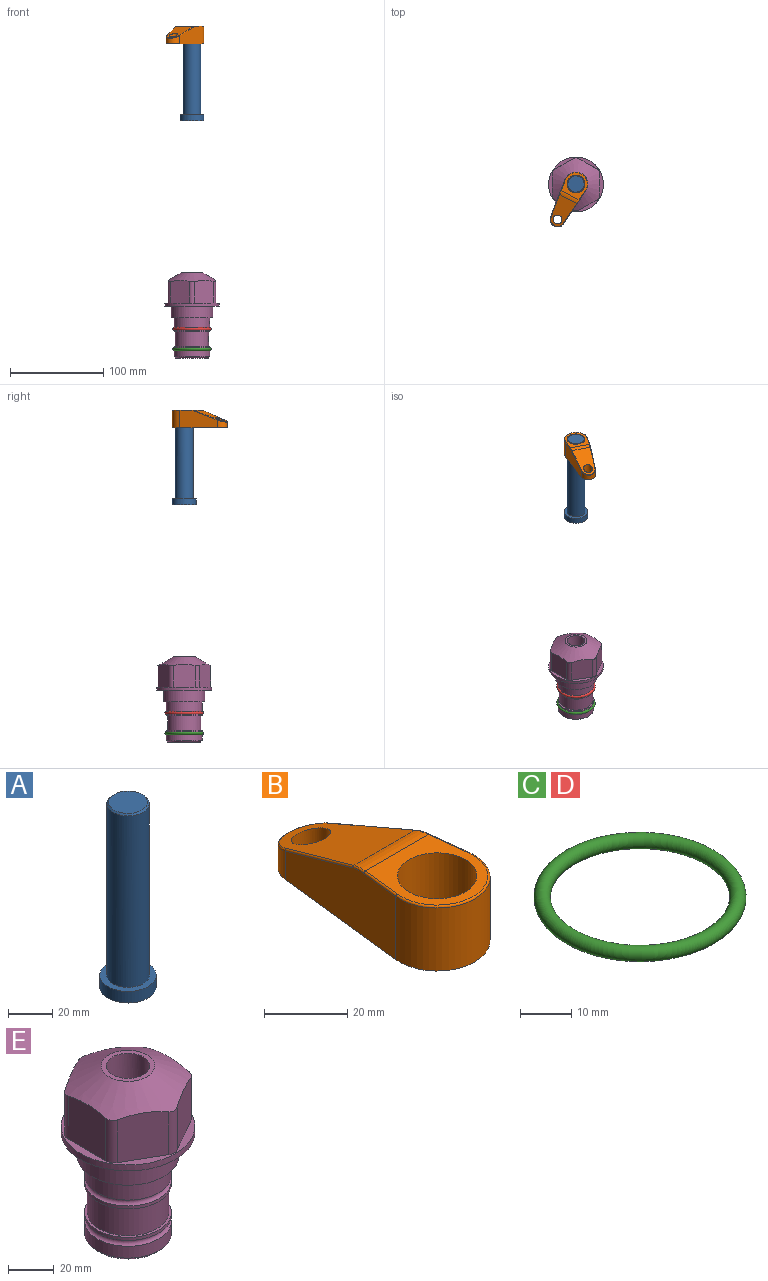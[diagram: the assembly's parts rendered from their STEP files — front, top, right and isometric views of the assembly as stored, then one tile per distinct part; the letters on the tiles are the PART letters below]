
ASSEMBLY  parts=5 mates=3
PART A: 6 faces, bbox 25.4x25.4x101.6 mm
  f0: plane 17.46x17.46mm, normal (0,0,1), area 239.5mm2, adj f5
  f1: plane 25.4x25.4mm, normal (0,0,-1), area 506.7mm2, adj f2
  f2: cylinder r=12.7mm len=25.4mm, axis (0,0,1), area 506.7mm2, adj f1,f3
  f3: plane 25.4x25.4mm, normal (0,0,1), area 221.7mm2, adj f2,f4
  f4: cylinder r=9.53mm len=94.46mm, axis (0,0,1), area 5653mm2, adj f3,f5
  f5: cone r=8.73mm half-angle=45deg, axis (0,0,-1), area 64.4mm2, adj f0,f4
PART B: 44 faces, bbox 27.5x64.5x19.1 mm
  f0: plane 2.3x0.95mm, normal (0,0,-1), area 1mm2, adj f25,f30,f34
  f1: plane 63.5x25.4mm, normal (0,0,-1), area 561.7mm2, adj f2,f3,f4,f5,f6,f7,f19,f20
  f2: cylinder r=12.7mm len=25.4mm, axis (0,0,-1), area 792.2mm2, adj f1,f3,f5,f13
  f3: plane 42.33x18.54mm, normal (0.99,0.11,0), area 647mm2, adj f1,f2,f4,f11,f12,f14
  f4: cylinder r=7.94mm len=15.78mm, axis (0,0,-1), area 158.6mm2, adj f1,f3,f5,f16
  f5: plane 42.33x18.54mm, normal (-0.99,0.11,0), area 647mm2, adj f1,f2,f4,f15,f17,f18
  f6: cylinder r=9.53mm len=19.05mm, axis (0,0,-1), area 1140.1mm2, adj f1,f8
  f7: cylinder r=4.76mm len=10.98mm, axis (0,0,-1), area 276.1mm2, adj f1,f9
  f8: plane 25.83x24.38mm, normal (0,0,1), area 262.2mm2, adj f6,f10,f11,f13,f15
  f9: plane 32.49x20.55mm, normal (0,0.34,0.94), area 489.9mm2, adj f7,f10,f14,f16,f18
  f10: cylinder r=12.7mm len=21.49mm, axis (-1,0,0), area 93.2mm2, adj f8,f9,f12,f17
  f11: cylinder r=0.51mm len=12.34mm, axis (0.11,-0.99,0), area 9.9mm2, adj f3,f8,f12,f13
  f12: bspline ~7.62x1.64mm, area 3.5mm2, adj f3,f10,f11,f14
  f13: torus R=12.19mm, axis (0,0,1), area 33.6mm2, adj f2,f8,f11,f15
  f14: cylinder r=0.51mm len=26.01mm, axis (0.1,-0.93,0.34), area 21.6mm2, adj f3,f9,f12,f16
  f15: cylinder r=0.51mm len=12.34mm, axis (0.11,0.99,0), area 9.9mm2, adj f5,f8,f13,f17
  f16: bspline ~15.78x7.05mm, area 15.7mm2, adj f4,f9,f14,f18
  f17: bspline ~7.62x1.64mm, area 3.5mm2, adj f5,f10,f15,f18
  f18: cylinder r=0.51mm len=26.01mm, axis (0.1,0.93,-0.34), area 21.6mm2, adj f5,f9,f16,f17
  f19: plane 21.6x14.29mm, normal (-0.99,-0.11,0), area 242.6mm2, adj f1,f26,f28,f34,f36,f38
  f20: plane 21.6x14.29mm, normal (0.99,-0.11,0), area 242.6mm2, adj f1,f27,f29,f37,f39,f41
  f21: cylinder r=12.7mm len=14.29mm, axis (0,0,-1), area 173.2mm2, adj f1,f26,f27,f30,f31,f33
  f22: cylinder r=7.94mm len=7.63mm, axis (0,0,-1), area 53.8mm2, adj f1,f28,f29,f42
  f23: plane 2.3x0.95mm, normal (0,0,-1), area 1mm2, adj f25,f33,f37
  f24: plane 17.94x12.32mm, normal (0,-0.34,-0.94), area 191.2mm2, adj f25,f38,f41,f42
  f25: cylinder r=9.53mm len=12.93mm, axis (-1,0,0), area 37.5mm2, adj f0,f23,f24,f31,f36,f39
  f26: cylinder r=1.59mm len=14.29mm, axis (0,0,-1), area 49mm2, adj f1,f19,f21,f32
  f27: cylinder r=1.59mm len=14.29mm, axis (0,0,-1), area 49mm2, adj f1,f20,f21,f35
  f28: cylinder r=1.59mm len=7.28mm, axis (0,0,-1), area 22.1mm2, adj f1,f19,f22,f40
  f29: cylinder r=1.59mm len=7.28mm, axis (0,0,-1), area 22.1mm2, adj f1,f20,f22,f43
  f30: torus R=14.29mm, axis (0,0,1), area 5.8mm2, adj f0,f21,f31,f32
  f31: bspline ~11.06x2.73mm, area 20.8mm2, adj f21,f25,f30,f33
  f32: sphere r=1.59mm, area 5.4mm2, adj f26,f30,f34
  f33: torus R=14.29mm, axis (0,0,1), area 5.8mm2, adj f21,f23,f31,f35
  f34: cylinder r=1.59mm len=1.68mm, axis (-0.11,0.99,0), area 2.4mm2, adj f0,f19,f32,f36
  f35: sphere r=1.59mm, area 5.4mm2, adj f27,f33,f37
  f36: bspline ~5.82x2.33mm, area 7.7mm2, adj f19,f25,f34,f38
  f37: cylinder r=1.59mm len=1.68mm, axis (0.11,0.99,0), area 2.4mm2, adj f20,f23,f35,f39
  f38: cylinder r=1.59mm len=18.33mm, axis (0.1,-0.93,0.34), area 46.7mm2, adj f19,f24,f36,f40
  f39: bspline ~5.82x2.33mm, area 7.7mm2, adj f20,f25,f37,f41
  f40: sphere r=1.59mm, area 3.6mm2, adj f28,f38,f42
  f41: cylinder r=1.59mm len=18.33mm, axis (0.1,0.93,-0.34), area 46.7mm2, adj f20,f24,f39,f43
  f42: bspline ~8.31x1.84mm, area 15.3mm2, adj f22,f24,f40,f43
  f43: sphere r=1.59mm, area 3.6mm2, adj f29,f41,f42
PART C: 1 faces, bbox 44.7x44.7x3.2 mm
  f0: torus R=19.05mm, axis (0,0,1), area 1193.9mm2
PART D: same geometry as C
PART E: 36 faces, bbox 58.7x58.7x91.2 mm
  f0: cylinder r=17.78mm len=35.56mm, axis (0,0,1), area 1670.8mm2, adj f23,f24,f31
  f1: cylinder r=19.05mm len=38.1mm, axis (0,0,1), area 1191.9mm2, adj f26,f27,f30
  f2: plane 58.66x58.66mm, normal (0,0,-1), area 1150.6mm2, adj f3,f28
  f3: cylinder r=29.33mm len=58.66mm, axis (0,0,-1), area 585.1mm2, adj f2,f4
  f4: plane 58.66x58.66mm, normal (0,0,1), area 475.9mm2, adj f3,f5,f6,f7,f8,f9,f10,f11
  f5: plane 24.5x20.32mm, normal (-0.5,0.87,0), area 562.8mm2, adj f4,f15,f16,f17
  f6: plane 24.5x20.32mm, normal (0.5,0.87,0), area 562.8mm2, adj f4,f14,f15,f17
  f7: plane 24.5x23.48mm, normal (1,0,0), area 562.8mm2, adj f4,f13,f14,f17
  f8: plane 24.5x20.32mm, normal (0.5,-0.87,0), area 562.8mm2, adj f4,f12,f13,f17
  f9: plane 24.5x20.32mm, normal (-0.5,-0.87,0), area 562.8mm2, adj f4,f11,f12,f17
  f10: plane 24.5x23.48mm, normal (-1,0,0), area 562.8mm2, adj f4,f11,f16,f17
  f11: cylinder r=5.08mm len=23.01mm, axis (0,0,-1), area 121.2mm2, adj f4,f9,f10,f17
  f12: cylinder r=5.08mm len=23.01mm, axis (0,0,-1), area 121.2mm2, adj f4,f8,f9,f17
  f13: cylinder r=5.08mm len=23.01mm, axis (0,0,-1), area 121.2mm2, adj f4,f7,f8,f17
  f14: cylinder r=5.08mm len=23.01mm, axis (0,0,-1), area 121.2mm2, adj f4,f6,f7,f17
  f15: cylinder r=5.08mm len=23.01mm, axis (0,0,-1), area 121.2mm2, adj f4,f5,f6,f17
  f16: cylinder r=5.08mm len=23.01mm, axis (0,0,-1), area 121.2mm2, adj f4,f5,f10,f17
  f17: cone r=11.73mm half-angle=60deg, axis (0,0,-1), area 2071.8mm2, adj f5,f6,f7,f8,f9,f10,f11,f12
  f18: plane 23.46x23.46mm, normal (0,0,1), area 147.4mm2, adj f17,f35
  f19: plane 34.93x34.93mm, normal (0,0,-1), area 958mm2, adj f29
  f20: cylinder r=19.05mm len=38.1mm, axis (0,0,1), area 760.1mm2, adj f21,f29
  f21: torus R=19.05mm, axis (0,0,1), area 565.3mm2, adj f20,f22
  f22: cylinder r=19.05mm len=38.1mm, axis (0,0,1), area 190mm2, adj f21,f23
  f23: plane 38.1x38.1mm, normal (0,0,1), area 146.9mm2, adj f0,f22
  f24: plane 38.1x38.1mm, normal (0,0,-1), area 146.9mm2, adj f0,f25
  f25: cylinder r=19.05mm len=38.1mm, axis (0,0,1), area 190mm2, adj f24,f26
  f26: torus R=19.05mm, axis (0,0,1), area 565.3mm2, adj f1,f25
  f27: plane 44.45x44.45mm, normal (0,0,-1), area 411.7mm2, adj f1,f28
  f28: cylinder r=22.23mm len=44.45mm, axis (0,0,1), area 1773.5mm2, adj f2,f27
  f29: cone r=19.05mm half-angle=45deg, axis (0,0,1), area 257.5mm2, adj f19,f20
  f30: cylinder r=3.17mm len=6.75mm, axis (-1,0,0), area 128mm2, adj f1,f33
  f31: cylinder r=3.17mm len=6.35mm, axis (-1,0,0), area 102.5mm2, adj f0,f33
  f32: plane 25.4x25.4mm, normal (0,0,1), area 506.7mm2, adj f33
  f33: cylinder r=12.7mm len=66.42mm, axis (0,0,-1), area 5236.2mm2, adj f30,f31,f32,f34
  f34: cone r=9.53mm half-angle=30deg, axis (0,0,-1), area 443.4mm2, adj f33,f35
  f35: cylinder r=9.53mm len=19.05mm, axis (0,0,-1), area 849mm2, adj f18,f34
PLACE A rot(axis=(0,0,-1),117.5deg) t=(0,0,226.62)mm
PLACE B rot(axis=(0,0,1),152.5deg) t=(0,0,281.23)mm
PLACE C t=(0,0,-21.59)mm
PLACE D at identity
PLACE E at identity fixed
MATE fastened C.f0 <-> E.f0  axis (0,0,1) through (0,0,-46.1)mm
MATE cylindrical A.f2 <-> E.f0  axis (0,0,1) through (0,0,252.26)mm
MATE fastened B.f2 <-> A.f2  axis (0,0,1) through (0,0,300.28)mm
